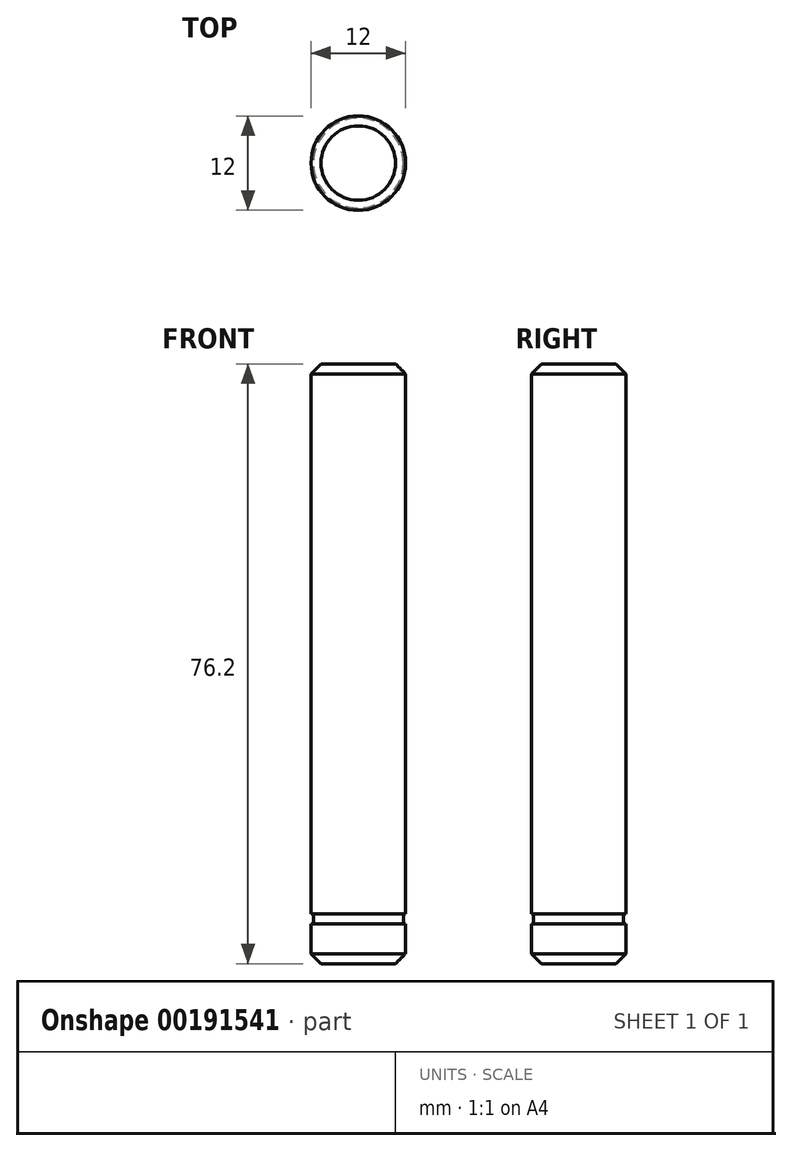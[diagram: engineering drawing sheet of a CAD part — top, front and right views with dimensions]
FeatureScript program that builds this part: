
annotation { "Feature Type Name" : "Feature", "Feature Type Description" : "" }
export const myFeature = defineFeature(function(context is Context, id is Id, definition is map)
    precondition{}
    {
        {
            var Q0;
            Q0=qCreatedBy(makeId("Top.planeOp"),FACE);
            var sketch = newSketch(context, id + "F0", { "sketchPlane" : qUnion([Q0])});
            skCircle(sketch, "E0", {"center": v(0, 0) * mm, "radius": 6 * mm});
            skSolve(sketch);
        }
        {
            var Q0;
            Q0 = qSketchRegion(id + "F0", true);
            extrude(context, id + "F1", {"entities" : qUnion([Q0]), "depth" : 76.2 * mm});
        }
        {
            var Q0;
            Q0=makeQuery(id+"F1.opExtrude","CAP_FACE",FACE,{"disambiguationData":[OSD([sQuery(id+"F0.wireOp",EDGE,"E0")])],"isStart":true});
            cPlane(context, id + "F2", {"entities" : qUnion([Q0]), "cplaneType" : CPlaneType.OFFSET, "offset" : 6.35 * mm, "oppositeDirection" : true, "width" : 152.4 * mm, "height" : 152.4 * mm});
        }
        {
            var Q0;
            Q0=qCreatedBy(id+"F2.planeOp",FACE);
            var sketch = newSketch(context, id + "F3", { "sketchPlane" : qUnion([Q0])});
            skCircle(sketch, "E1.0", {"center": v(0, 0) * mm, "radius": 6 * mm});
            skCircle(sketch, "E2", {"center": v(0, 0) * mm, "radius": 5.72 * mm});
            skSolve(sketch);
        }
        {
            var Q0;
            Q0 = qSketchRegion(id + "F3", true);
            extrude(context, id + "F4", {"entities" : qUnion([Q0]), "operationType" : NewBodyOperationType.REMOVE, "depth" : 1.27 * mm});
        }
        {
            var Q0;
            Q0=makeQuery(id+"F1.opExtrude","CAP_EDGE",EDGE,{"disambiguationData":[OSD([sQuery(id+"F0.wireOp",EDGE,"E0")])],"isStart":true});
            var Q1;
            Q1=makeQuery(id+"F1.opExtrude","CAP_EDGE",EDGE,{"disambiguationData":[OSD([sQuery(id+"F0.wireOp",EDGE,"E0")])],"isStart":false});
            chamfer(context, id + "F5", {"entities" : qUnion([Q0, Q1]), "width" : 1.27 * mm, "tangentPropagation" : true});
        }
    });
